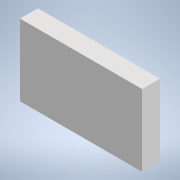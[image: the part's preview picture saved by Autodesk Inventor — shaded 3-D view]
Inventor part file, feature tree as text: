
AUTODESK INVENTOR PART (.ipt)
format: ipt  version: 2020 (Build 240168000, 168)  size: 90,112 bytes
history: native  units: in
note: dims shown in document units (in); Inventor stores cm internally (conversion verified against a paired STEP export)
features: other x5, extrude x1, sketch x1, reference x1
ambient origin geometry x8: Origin, YZ Plane, XZ Plane, XY Plane, X Axis, Y Axis, Z Axis, Center Point
bodies: Body1 (feature_tree)
feature tree (8):
  extrude  "Extrusion2"  Depth=0.25in
  sketch  "Sketch1"  dims[d0=0.5in d1=0.5in d4=2.0in d5=0.25in d6=0.0in]
  reference  "Reference1"
  other  "<userpath>\Documents\Inventor\Drone\Assembly.iam"
  other  "Assembly.iam"
  other  "Frame:1"
  other  "DJI F330 qoadrotor arm:2"
  other  "DJI F330 qoadrotor arm v2"
